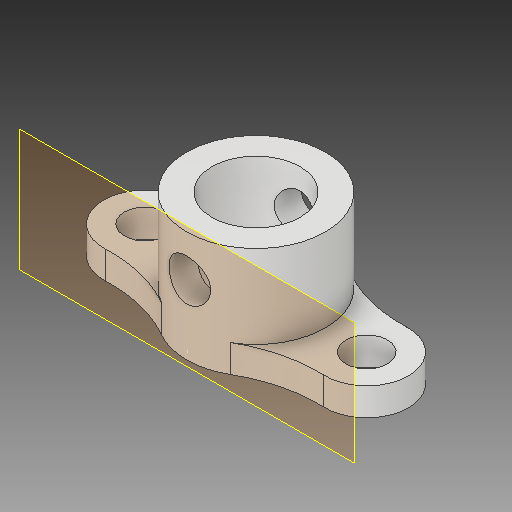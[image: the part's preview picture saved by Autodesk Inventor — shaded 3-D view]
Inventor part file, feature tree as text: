
AUTODESK INVENTOR PART (.ipt)
format: ipt  version: 2018 (Build 220112000, 112)  size: 168,448 bytes
history: native  units: mm
features: extrude x3, sketch x2, plane x1
ambient origin geometry x8: Origin, YZ Plane, XZ Plane, XY Plane, X Axis, Y Axis, Z Axis, Center Point
bodies: Solid1 (feature_tree)
feature tree (6):
  sketch  "Sketch1"  dims[d0=6.35mm d1=10.0mm]
  extrude  "Extrusion1"  Depth=10.0mm
  extrude  "Extrusion2"  Depth=3.0mm
  extrude  "Extrusion3"  Depth=10.0mm
  plane  "Work Plane1"
  sketch  "Sketch2"  dims[d2=3.0mm d3=3.0mm d4=8.0mm d5=8.0mm d6=3.0mm d7=2.0mm d8=0.0mm d9=6.0mm d10=0.0mm d11=3.0mm d12=6.0mm d13=0.0mm d14=10.0mm]
